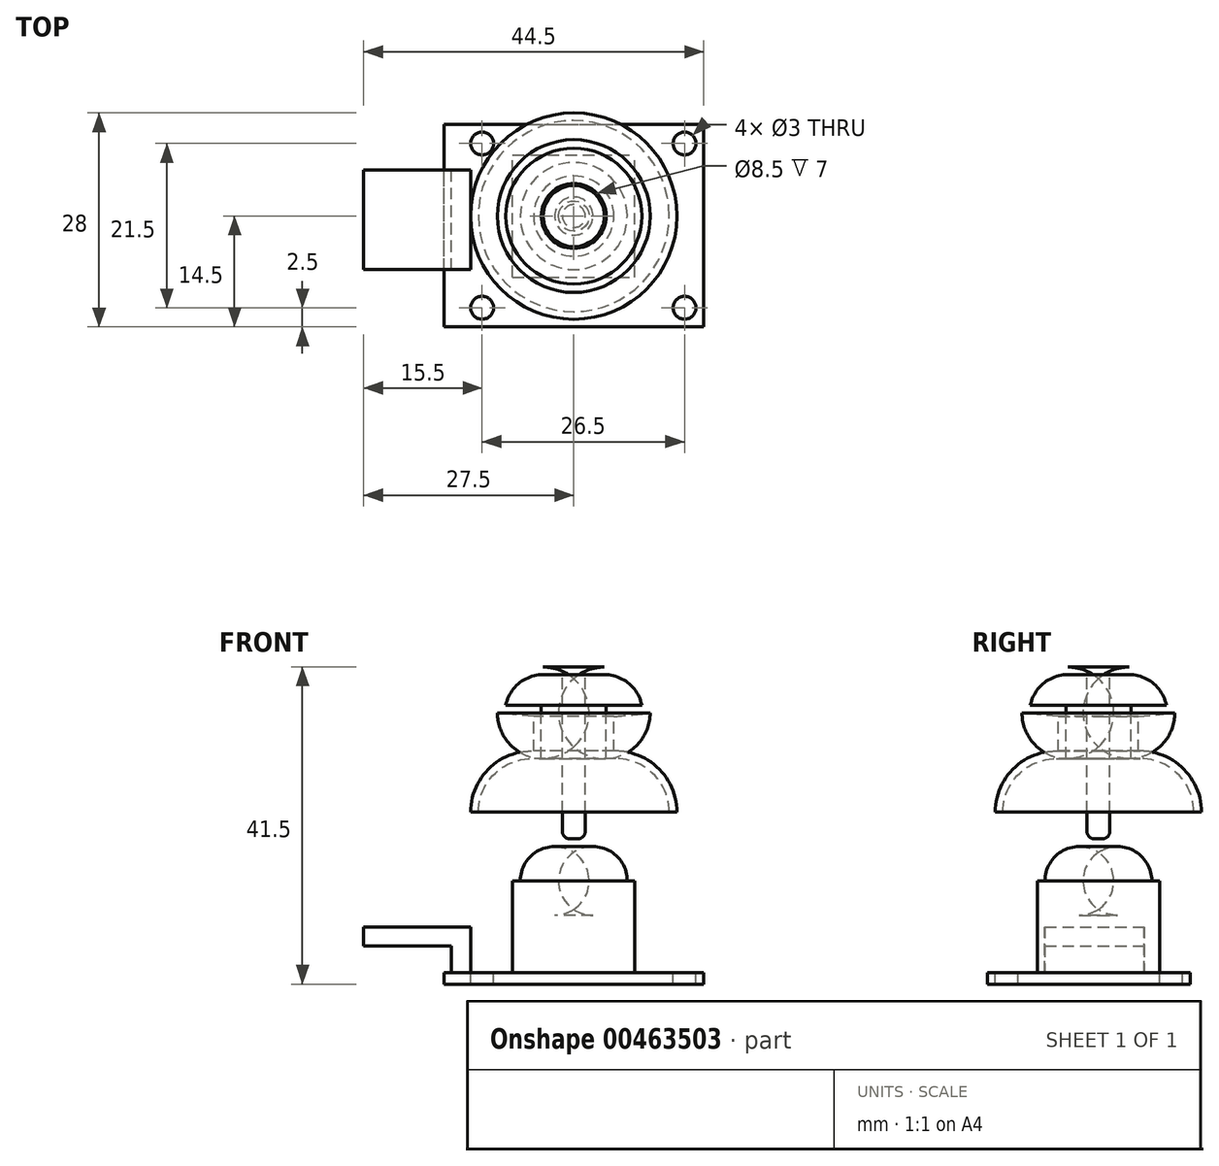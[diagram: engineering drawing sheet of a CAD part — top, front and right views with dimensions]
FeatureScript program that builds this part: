
annotation { "Feature Type Name" : "Feature", "Feature Type Description" : "" }
export const myFeature = defineFeature(function(context is Context, id is Id, definition is map)
    precondition{}
    {
        {
            var Q0;
            Q0=qCreatedBy(makeId("Front.planeOp"),FACE);
            var sketch = newSketch(context, id + "F0", { "sketchPlane" : qUnion([Q0])});
            skLineSegment(sketch, "E0", {"start": v(0, -19) * mm, "end": v(13.5, -19) * mm});
            skLineSegment(sketch, "E1", {"start": v(13.5, -19) * mm, "end": v(13.5, -19) * mm});
            skLineSegment(sketch, "E2", {"start": v(5.5, -11) * mm, "end": v(5.25, -11) * mm});
            skLineSegment(sketch, "E3", {"start": v(5.25, -11) * mm, "end": v(5.25, -6) * mm});
            skLineSegment(sketch, "E4", {"start": v(5.25, -6) * mm, "end": v(10, -6) * mm});
            skLineSegment(sketch, "E5", {"start": v(10, -6) * mm, "end": v(10, -6) * mm});
            skLineSegment(sketch, "E6", {"start": v(4, 0) * mm, "end": v(0, 0) * mm});
            skPoint(sketch, "E7.visualSharp", {"position": v(13.5, -11) * mm});
            skArc(sketch, "E7.filletArc", {"start": v(13.5, -19) * mm, "mid": v(11.16, -13.34) * mm, "end": v(5.5, -11) * mm});
            skPoint(sketch, "E8.visualSharp", {"position": v(10, 0) * mm});
            skArc(sketch, "E8.filletArc", {"start": v(10, -6) * mm, "mid": v(8.24, -1.76) * mm, "end": v(4, 0) * mm});
            skLineSegment(sketch, "E9", {"start": v(0, 0) * mm, "end": v(0, -19) * mm});
            skSolve(sketch);
        }
        {
            var Q0;
            Q0=makeQuery(id+"F0.imprint","IMPRINT",FACE,{"disambiguationData":[TD([[makeQuery(id+"F0.imprint","IMPRINT",EDGE,{"derivedFrom":sQuery(id+"F0.wireOp",EDGE,"E0")}),1.0]])]});
            var Q1;
            Q1=sQuery(id+"F0.wireOp",EDGE,"E9");
            revolve(context, id + "F1", {"entities" : qUnion([Q0]), "axis" : qUnion([Q1]), "revolveType" : RevolveType.FULL});
        }
        {
            var Q0;
            Q0=makeQuery(id+"F1.opRevolve","SWEPT_FACE",FACE,{"disambiguationData":[OSD([sQuery(id+"F0.wireOp",EDGE,"E0")])]});
            shell(context, id + "F2", {"entities" : qUnion([Q0]), "thickness" : 1 * mm});
        }
        {
            var Q0;
            Q0=makeQuery(id+"F2.opShell","OFFSET_FACE",FACE,{"disambiguationData":[OSD([sQuery(id+"F0.wireOp",EDGE,"E6")])]});
            var sketch = newSketch(context, id + "F3", { "sketchPlane" : qUnion([Q0])});
            skCircle(sketch, "E10", {"center": v(0, 0) * mm, "radius": 1.5 * mm});
            skSolve(sketch);
        }
        {
            var Q0;
            Q0=makeQuery(id+"F3.imprint","IMPRINT",FACE,{"disambiguationData":[TD([[makeQuery(id+"F3.imprint","IMPRINT",EDGE,{"derivedFrom":sQuery(id+"F3.wireOp",EDGE,"E10")}),1.0]])]});
            extrude(context, id + "F4", {"entities" : qUnion([Q0]), "operationType" : NewBodyOperationType.ADD, "depth" : 21.5 * mm});
        }
        {
            var Q0;
            Q0=makeQuery(id+"F1.opRevolve","SWEPT_EDGE",EDGE,{"disambiguationData":[OSD([sQuery(id+"F0.wireOp",EDGE,"E3"),sQuery(id+"F0.wireOp",EDGE,"E4")])]});
            chamfer(context, id + "F5", {"entities" : qUnion([Q0]), "chamferType" : ChamferType.TWO_OFFSETS, "width1" : 5 * mm, "oppositeDirection" : false, "width2" : 0.5 * mm, "tangentPropagation" : true});
        }
        {
            var Q0;
            Q0=qCreatedBy(makeId("Front.planeOp"),FACE);
            var sketch = newSketch(context, id + "F6", { "sketchPlane" : qUnion([Q0])});
            skLineSegment(sketch, "E11.bottom", {"start": v(-8, -28) * mm, "end": v(8, -28) * mm});
            skLineSegment(sketch, "E11.top", {"start": v(-8, -40) * mm, "end": v(8, -40) * mm});
            skLineSegment(sketch, "E11.left", {"start": v(-8, -28) * mm, "end": v(-8, -40) * mm});
            skLineSegment(sketch, "E11.right", {"start": v(8, -28) * mm, "end": v(8, -40) * mm});
            skSolve(sketch);
        }
        {
            var Q0;
            Q0=makeQuery(id+"F6.imprint","IMPRINT",FACE,{"disambiguationData":[TD([[makeQuery(id+"F6.imprint","IMPRINT",EDGE,{"derivedFrom":sQuery(id+"F6.wireOp",EDGE,"E11.bottom")}),-1.0]])]});
            extrude(context, id + "F7", {"entities" : qUnion([Q0]), "operationType" : NewBodyOperationType.ADD, "depth" : 16 * mm, "symmetric" : true});
        }
        {
            var Q0;
            Q0=makeQuery(id+"F4.opExtrude","CAP_EDGE",EDGE,{"disambiguationData":[OSD([sQuery(id+"F3.wireOp",EDGE,"E10")])],"isStart":false});
            fillet(context, id + "F8", {"entities" : qUnion([Q0]), "radius" : 1 * mm, "tangentPropagation" : true, "allowEdgeOverflow" : false});
        }
        {
            var Q0;
            Q0=makeQuery(id+"F7.opExtrude","SWEPT_FACE",FACE,{"disambiguationData":[OSD([sQuery(id+"F6.wireOp",EDGE,"E11.top")])]});
            var sketch = newSketch(context, id + "F9", { "sketchPlane" : qUnion([Q0])});
            skLineSegment(sketch, "E12.bottom", {"start": v(-17, 14.5) * mm, "end": v(17, 14.5) * mm});
            skLineSegment(sketch, "E12.top", {"start": v(-17, -12) * mm, "end": v(17, -12) * mm});
            skLineSegment(sketch, "E12.left", {"start": v(-17, 14.5) * mm, "end": v(-17, -12) * mm});
            skLineSegment(sketch, "E12.right", {"start": v(17, 14.5) * mm, "end": v(17, -12) * mm});
            skCircle(sketch, "E13", {"center": v(14.5, 12) * mm, "radius": 1.5 * mm});
            skCircle(sketch, "E14", {"center": v(14.5, -9.5) * mm, "radius": 1.5 * mm});
            skCircle(sketch, "E15", {"center": v(-12, -9.5) * mm, "radius": 1.5 * mm});
            skCircle(sketch, "E16", {"center": v(-12, 12) * mm, "radius": 1.5 * mm});
            skSolve(sketch);
        }
        {
            var Q0;
            Q0=makeQuery(id+"F9.imprint","IMPRINT",FACE,{"disambiguationData":[TD([[makeQuery(id+"F9.imprint","IMPRINT",EDGE,{"derivedFrom":sQuery(id+"F9.wireOp",EDGE,"E12.bottom")}),-1.0]])]});
            var Q1;
            {var subQ0=sQuery(id+"F6.wireOp",EDGE,"E11.top");Q1=makeQuery(id+"F9.imprint","IMPRINT",FACE,{"disambiguationData":[TD([[makeQuery(id+"F9.imprint","IMPRINT",EDGE,{"derivedFrom":makeQuery(id+"F7.opExtrude","CAP_EDGE",EDGE,{"disambiguationData":[OSD([subQ0])],"isStart":true})}),1.0]])]});}
            extrude(context, id + "F10", {"entities" : qUnion([Q0, Q1]), "depth" : 1.5 * mm});
        }
        {
            var Q0;
            Q0=qCreatedBy(makeId("Front.planeOp"),FACE);
            var sketch = newSketch(context, id + "F11", { "sketchPlane" : qUnion([Q0])});
            skLineSegment(sketch, "E17", {"start": v(-13.5, -40) * mm, "end": v(-13.5, -34) * mm});
            skLineSegment(sketch, "E18", {"start": v(-13.5, -34) * mm, "end": v(-27.5, -34) * mm});
            skLineSegment(sketch, "E19", {"start": v(-27.5, -34) * mm, "end": v(-27.5, -36.5) * mm});
            skLineSegment(sketch, "E20", {"start": v(-27.5, -36.5) * mm, "end": v(-16, -36.5) * mm});
            skLineSegment(sketch, "E21", {"start": v(-16, -36.5) * mm, "end": v(-16, -40) * mm});
            skLineSegment(sketch, "E22", {"start": v(-16, -40) * mm, "end": v(-13.5, -40) * mm});
            skSolve(sketch);
        }
        {
            var Q0;
            Q0=makeQuery(id+"F11.imprint","IMPRINT",FACE,{"disambiguationData":[TD([[makeQuery(id+"F11.imprint","IMPRINT",EDGE,{"derivedFrom":sQuery(id+"F11.wireOp",EDGE,"E17")}),1.0]])]});
            extrude(context, id + "F12", {"entities" : qUnion([Q0]), "operationType" : NewBodyOperationType.ADD, "depth" : 7 * mm, "hasSecondDirection" : true, "secondDirectionOppositeDirection" : true, "secondDirectionDepth" : 6 * mm});
        }
        {
            var Q0;
            Q0=makeQuery(id+"F7.opExtrude","SWEPT_FACE",FACE,{"disambiguationData":[OSD([sQuery(id+"F6.wireOp",EDGE,"E11.bottom")])]});
            var sketch = newSketch(context, id + "F13", { "sketchPlane" : qUnion([Q0])});
            skCircle(sketch, "E23", {"center": v(0, 0) * mm, "radius": 7 * mm});
            skSolve(sketch);
        }
        {
            var Q0;
            Q0=makeQuery(id+"F13.imprint","IMPRINT",FACE,{"disambiguationData":[TD([[makeQuery(id+"F13.imprint","IMPRINT",EDGE,{"derivedFrom":sQuery(id+"F13.wireOp",EDGE,"E23")}),1.0]])]});
            extrude(context, id + "F14", {"entities" : qUnion([Q0]), "operationType" : NewBodyOperationType.REMOVE, "oppositeDirection" : true, "depth" : 4.5 * mm});
        }
        {
            var Q0;
            Q0=makeQuery(id+"F14.boolean.opBoolean","COPY",EDGE,{"derivedFrom":makeQuery(id+"F14.opExtrude","CAP_EDGE",EDGE,{"disambiguationData":[OSD([sQuery(id+"F13.wireOp",EDGE,"E23")])],"isStart":false})});
            fillet(context, id + "F15", {"entities" : qUnion([Q0]), "radius" : 4.5 * mm, "tangentPropagation" : true, "allowEdgeOverflow" : false});
        }
    });
